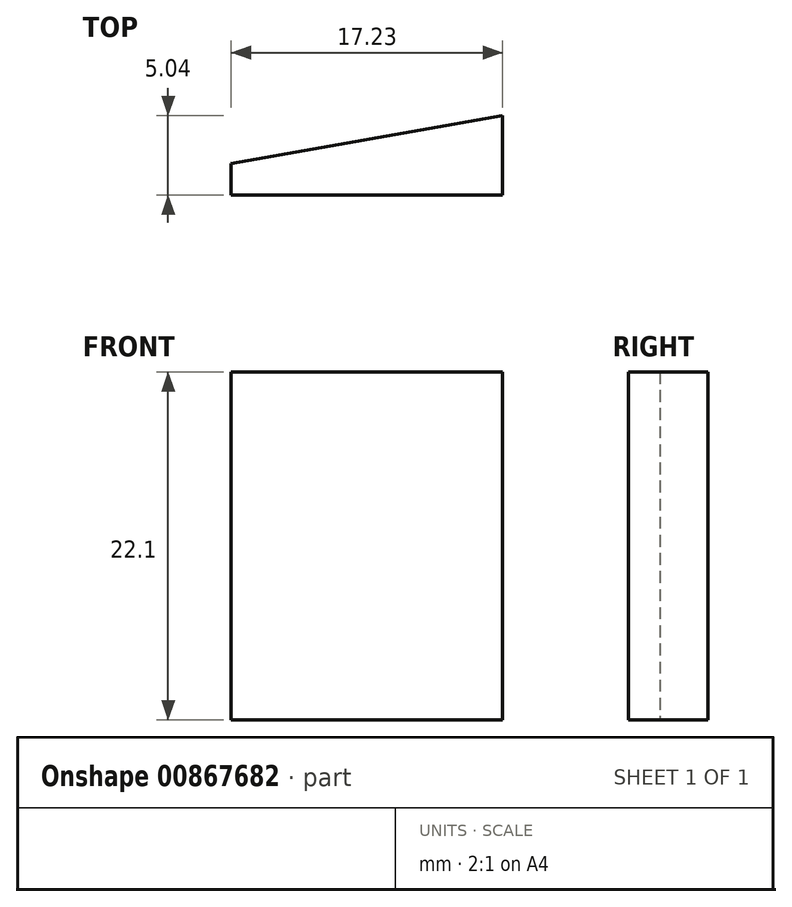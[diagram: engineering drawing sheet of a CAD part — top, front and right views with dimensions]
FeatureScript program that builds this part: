
annotation { "Feature Type Name" : "Feature", "Feature Type Description" : "" }
export const myFeature = defineFeature(function(context is Context, id is Id, definition is map)
    precondition{}
    {
        {
            var Q0;
            Q0=qCreatedBy(makeId("Top.planeOp"),FACE);
            var sketch = newSketch(context, id + "F0", { "sketchPlane" : qUnion([Q0])});
            skLineSegment(sketch, "E0", {"start": v(0, 0) * mm, "end": v(17.23, 0) * mm});
            skLineSegment(sketch, "E1", {"start": v(17.23, 0) * mm, "end": v(17.23, 3.04) * mm});
            skLineSegment(sketch, "E2", {"start": v(17.23, 3.04) * mm, "end": v(0, 0) * mm});
            skSolve(sketch);
        }
        {
            var Q0;
            Q0=makeQuery(id+"F0.imprint","IMPRINT",FACE,{"disambiguationData":[TD([[makeQuery(id+"F0.imprint","IMPRINT",EDGE,{"derivedFrom":sQuery(id+"F0.wireOp",EDGE,"E0")}),1.0]])]});
            extrude(context, id + "F1", {"entities" : qUnion([Q0]), "depth" : 22.1 * mm, "offsetDistance" : 25 * mm});
        }
        {
            var Q0;
            Q0=makeQuery(id+"F1.opExtrude","SWEPT_FACE",FACE,{"disambiguationData":[OSD([sQuery(id+"F0.wireOp",EDGE,"E0")])]});
            extrude(context, id + "F2", {"entities" : qUnion([Q0]), "operationType" : NewBodyOperationType.ADD, "depth" : 2 * mm, "offsetDistance" : 25 * mm});
        }
    });
